# Revit family: POC-Suspension
name_source: partatom
category: Lighting Fixtures
units: mm (PartAtom-declared; Revit-internal decimal feet)

## family parameters
Always vertical = Yes
Cut with Voids When Loaded = No
Host = Ceiling
Light Source = No
OmniClass Number = 23.80.70.11
OmniClass Title = Luminaries for Internal Lighting
Part Type = Normal
Room Calculation Point = No
Round Connector Dimension = Use Diameter
Shared = No

## types (2) — shared parameters
Bulb Diametr = 15 mm  [stored 0.0492126 ft]
Description = SUSPENSION
Designer = Studio Debonademeo
Manufacturer = Vistosi
Manufacturer country = Italy
Model = POC
Type Comments = Studio Debonademeo
URL = https://vistosi.com
URL Product Page = https://vistosi.it
Width = 25 mm  [stored 0.082021 ft]
zero-valued in all types: Default Elevation, Depth

## per-type parameters (varying)
| type | Lampshade Type | POC SP 25 |
| POC SP16 | POC_Lampshade : POC_D=160mm | No |
| POC SP25 | POC_Lampshade : POC_D=250mm | Yes |

note: [stored X ft] marks values corroborated as IEEE doubles in the binary element streams (Revit-internal decimal feet)

## geometry (parser evidence)
native form markers: Sweep x9
no freeform markers — native parametric forms only
